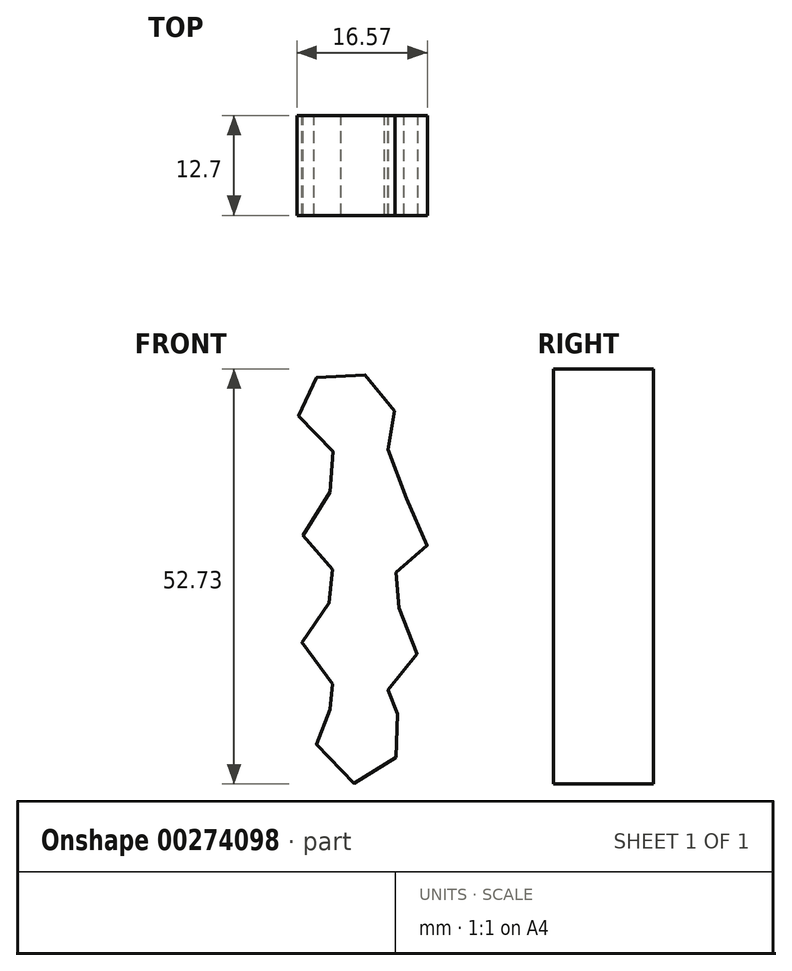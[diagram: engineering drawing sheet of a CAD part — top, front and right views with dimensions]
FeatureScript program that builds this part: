
annotation { "Feature Type Name" : "Feature", "Feature Type Description" : "" }
export const myFeature = defineFeature(function(context is Context, id is Id, definition is map)
    precondition{}
    {
        {
            var Q0;
            Q0=qCreatedBy(makeId("Front.planeOp"),FACE);
            var sketch = newSketch(context, id + "F0", { "sketchPlane" : qUnion([Q0])});
            skFitSpline(sketch, "E0", {"points": [v(6.82, 39.82) * mm, v(0, 45.17) * mm, v(-5.53, 39.64) * mm, v(0, 32.63) * mm, v(-4.8, 23.78) * mm, v(0, 17.88) * mm, v(-4.98, 10.7) * mm, v(0, 3.32) * mm, v(-3.32, 0) * mm, v(2.4, -7.56) * mm, v(7.93, 0) * mm, v(5.53, 3.5) * mm, v(9.77, 9.59) * mm, v(6.08, 18.07) * mm, v(10.88, 22.5) * mm, v(6.08, 33.18) * mm, v(6.82, 39.82) * mm]});
            skSolve(sketch);
        }
        {
            var Q0;
            Q0 = qSketchRegion(id + "F0", true);
            extrude(context, id + "F1", {"entities" : qUnion([Q0]), "depth" : 12.7 * mm});
        }
    });
